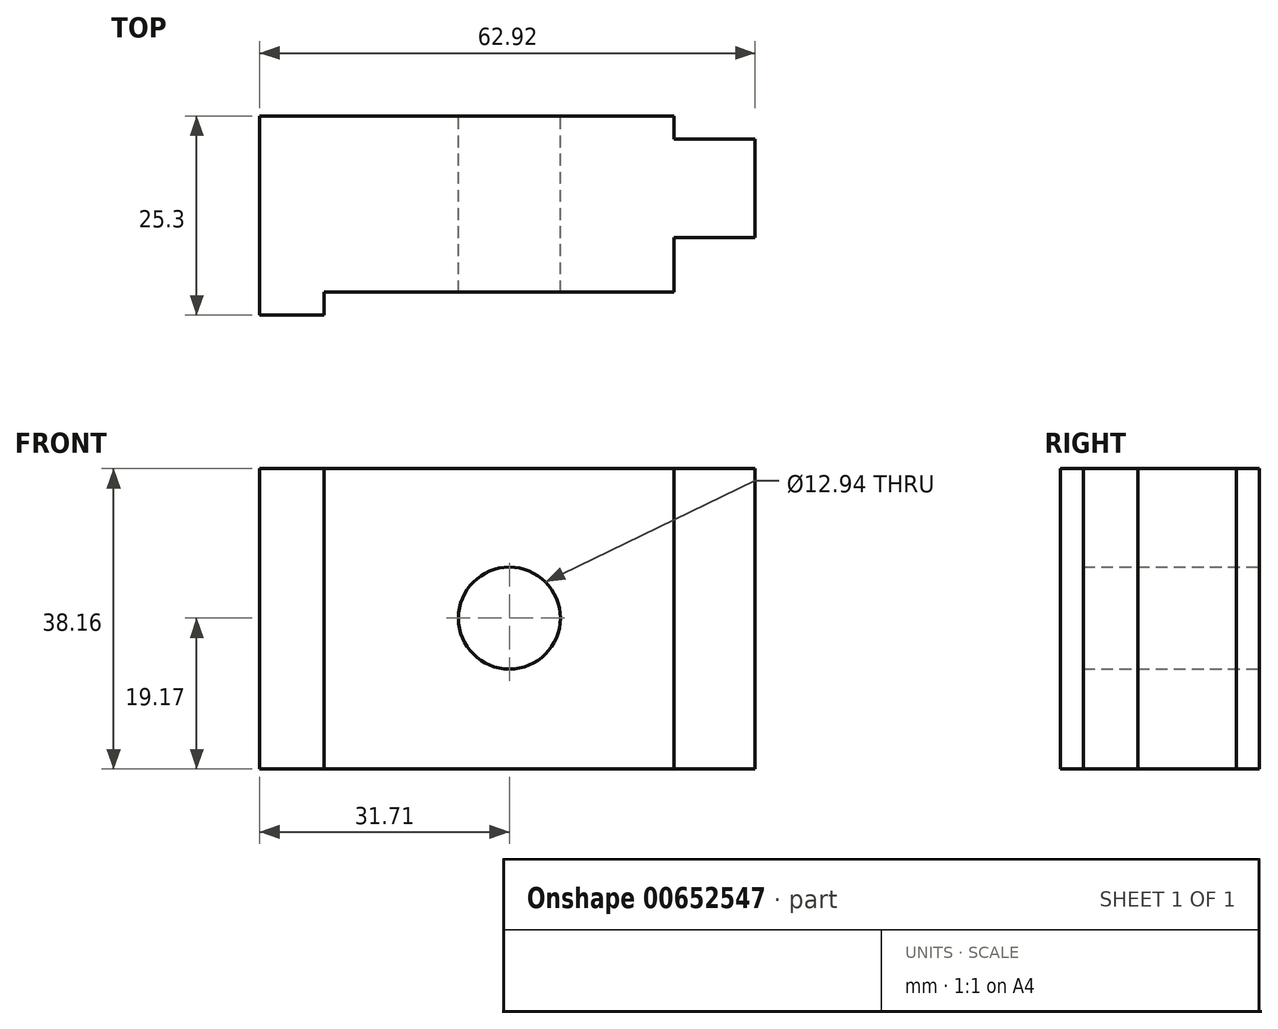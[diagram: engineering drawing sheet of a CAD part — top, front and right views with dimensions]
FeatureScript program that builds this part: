
annotation { "Feature Type Name" : "Feature", "Feature Type Description" : "" }
export const myFeature = defineFeature(function(context is Context, id is Id, definition is map)
    precondition{}
    {
        {
            var Q0;
            Q0=qCreatedBy(makeId("Front.planeOp"),FACE);
            var sketch = newSketch(context, id + "F0", { "sketchPlane" : qUnion([Q0])});
            skLineSegment(sketch, "E0.bottom", {"start": v(0, 0) * mm, "end": v(62.92, 0) * mm});
            skLineSegment(sketch, "E0.top", {"start": v(0, 38.16) * mm, "end": v(62.92, 38.16) * mm});
            skLineSegment(sketch, "E0.left", {"start": v(0, 0) * mm, "end": v(0, 38.16) * mm});
            skLineSegment(sketch, "E0.right", {"start": v(62.92, 0) * mm, "end": v(62.92, 38.16) * mm});
            skLineSegment(sketch, "E1", {"start": v(0, 0) * mm, "end": v(8.18, 0) * mm});
            skLineSegment(sketch, "E2", {"start": v(8.18, 0) * mm, "end": v(8.18, 38.16) * mm});
            skLineSegment(sketch, "E3", {"start": v(52.62, 38.16) * mm, "end": v(52.62, 0) * mm});
            skCircle(sketch, "E4", {"center": v(31.7, 19.17) * mm, "radius": 6.47 * mm});
            skSolve(sketch);
        }
        {
            var Q0;
            {var subQ0=sQuery(id+"F0.wireOp",EDGE,"E0.left");Q0=makeQuery(id+"F0.imprint","IMPRINT",FACE,{"disambiguationData":[TD([[makeQuery(id+"F0.imprint","IMPRINT",EDGE,{"derivedFrom":subQ0}),-1.0]])]});}
            extrude(context, id + "F1", {"entities" : qUnion([Q0]), "depth" : 25.3 * mm, "offsetDistance" : 25 * mm});
        }
        {
            var Q0;
            {var subQ1=sQuery(id+"F0.wireOp",EDGE,"E2");Q0=makeQuery(id+"F0.imprint","IMPRINT",FACE,{"disambiguationData":[TD([[makeQuery(id+"F0.imprint","IMPRINT",EDGE,{"derivedFrom":subQ1}),-1.0]])]});}
            extrude(context, id + "F2", {"entities" : qUnion([Q0]), "operationType" : NewBodyOperationType.ADD, "depth" : 22.4 * mm, "offsetDistance" : 25 * mm});
        }
        {
            var Q0;
            {var subQ0=sQuery(id+"F0.wireOp",EDGE,"E0.right");Q0=makeQuery(id+"F0.imprint","IMPRINT",FACE,{"disambiguationData":[TD([[makeQuery(id+"F0.imprint","IMPRINT",EDGE,{"derivedFrom":subQ0}),1.0]])]});}
            extrude(context, id + "F3", {"entities" : qUnion([Q0]), "operationType" : NewBodyOperationType.ADD, "depth" : 15.44 * mm, "offsetDistance" : 25 * mm, "hasSecondDirection" : true, "secondDirectionOppositeDirection" : true, "secondDirectionDepth" : -2.94 * mm});
        }
    });
